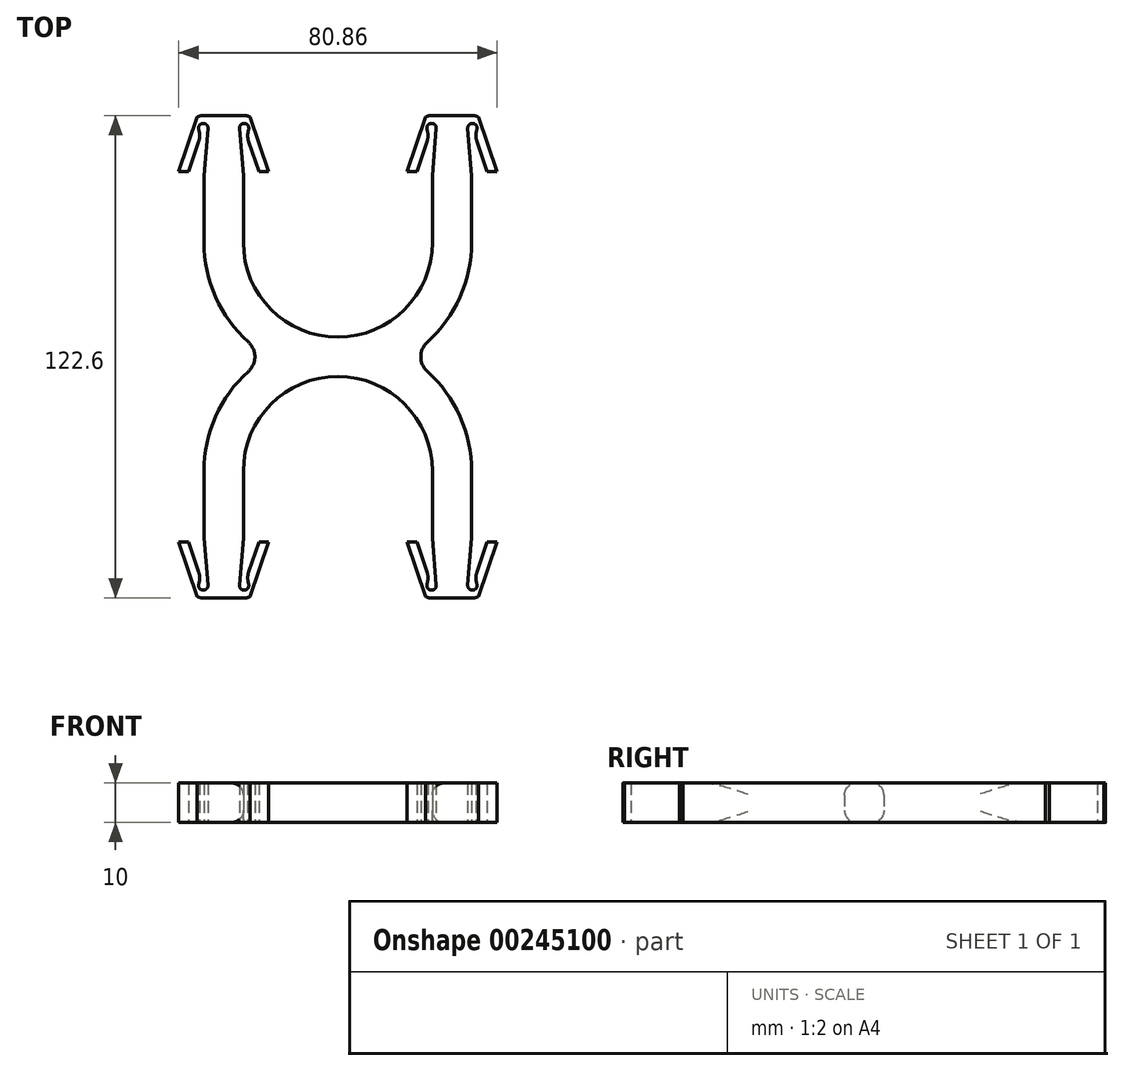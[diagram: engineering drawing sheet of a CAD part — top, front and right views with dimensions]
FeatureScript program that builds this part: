
annotation { "Feature Type Name" : "Feature", "Feature Type Description" : "" }
export const myFeature = defineFeature(function(context is Context, id is Id, definition is map)
    precondition{}
    {
        {
            var Q0;
            Q0=qCreatedBy(makeId("Top.planeOp"),FACE);
            var sketch = newSketch(context, id + "F0", { "sketchPlane" : qUnion([Q0])});
            skLineSegment(sketch, "E0", {"start": v(6.36, 8.63) * mm, "end": v(8.93, 1) * mm});
            skLineSegment(sketch, "E1", {"start": v(8.93, 1) * mm, "end": v(11.43, 1) * mm});
            skLineSegment(sketch, "E2", {"start": v(11.43, 1) * mm, "end": v(6.76, 14.9) * mm});
            skLineSegment(sketch, "E3", {"start": v(5.2, 15.3) * mm, "end": v(0, 15.3) * mm});
            skArc(sketch, "E4", {"start": v(6.34, 11.74) * mm, "mid": v(5.33, 13.3) * mm, "end": v(4, 12) * mm});
            skLineSegment(sketch, "E5", {"start": v(5, 0) * mm, "end": v(4, 12) * mm});
            skArc(sketch, "E6", {"start": v(5.2, 15.3) * mm, "mid": v(6, 15.2) * mm, "end": v(6.76, 14.9) * mm});
            skLineSegment(sketch, "E7.MirrorCS", {"start": v(-5.2, 15.3) * mm, "end": v(0, 15.3) * mm});
            skArc(sketch, "E8.MirrorCS", {"start": v(-5.2, 15.3) * mm, "mid": v(-6, 15.2) * mm, "end": v(-6.76, 14.9) * mm});
            skLineSegment(sketch, "E9.MirrorCS", {"start": v(-11.43, 1) * mm, "end": v(-6.76, 14.9) * mm});
            skLineSegment(sketch, "E10.MirrorCS", {"start": v(-8.93, 1) * mm, "end": v(-11.43, 1) * mm});
            skLineSegment(sketch, "E11.MirrorCS", {"start": v(-6.36, 8.63) * mm, "end": v(-8.93, 1) * mm});
            skArc(sketch, "E12.MirrorCS", {"start": v(-6.34, 11.74) * mm, "mid": v(-5.33, 13.3) * mm, "end": v(-4, 12) * mm});
            skLineSegment(sketch, "E13.MirrorCS", {"start": v(-5, 0) * mm, "end": v(-4, 12) * mm});
            skLineSegment(sketch, "E14", {"start": v(-5, 0) * mm, "end": v(-5, -17) * mm});
            skLineSegment(sketch, "E15.MirrorCS", {"start": v(5, 0) * mm, "end": v(5, -17) * mm});
            skArc(sketch, "E16", {"start": v(5, -17) * mm, "mid": v(29, -41) * mm, "end": v(53, -17) * mm});
            skArc(sketch, "E17", {"start": v(-5, -17) * mm, "mid": v(-2.06, -30.84) * mm, "end": v(6.27, -42.28) * mm});
            skLineSegment(sketch, "E18", {"start": v(29, -17) * mm, "end": v(29, -5.61) * mm, "construction": true});
            skLineSegment(sketch, "E19.MirrorCS", {"start": v(53, 0) * mm, "end": v(53, -17) * mm});
            skLineSegment(sketch, "E20.MirrorCS", {"start": v(63, 0) * mm, "end": v(63, -17) * mm});
            skLineSegment(sketch, "E21.MirrorCS", {"start": v(63, 0) * mm, "end": v(62, 12) * mm});
            skArc(sketch, "E22.MirrorCS", {"start": v(64.34, 11.74) * mm, "mid": v(63.33, 13.3) * mm, "end": v(62, 12) * mm});
            skLineSegment(sketch, "E23.MirrorCS", {"start": v(64.36, 8.63) * mm, "end": v(66.93, 1) * mm});
            skLineSegment(sketch, "E24.MirrorCS", {"start": v(66.93, 1) * mm, "end": v(69.43, 1) * mm});
            skLineSegment(sketch, "E25.MirrorCS", {"start": v(69.43, 1) * mm, "end": v(64.76, 14.9) * mm});
            skArc(sketch, "E26.MirrorCS", {"start": v(63.2, 15.3) * mm, "mid": v(64, 15.2) * mm, "end": v(64.76, 14.9) * mm});
            skLineSegment(sketch, "E27.MirrorCS", {"start": v(63.2, 15.3) * mm, "end": v(58, 15.3) * mm});
            skLineSegment(sketch, "E28.MirrorCS", {"start": v(52.8, 15.3) * mm, "end": v(58, 15.3) * mm});
            skArc(sketch, "E29.MirrorCS", {"start": v(52.8, 15.3) * mm, "mid": v(52, 15.2) * mm, "end": v(51.24, 14.9) * mm});
            skLineSegment(sketch, "E30.MirrorCS", {"start": v(46.57, 1) * mm, "end": v(51.24, 14.9) * mm});
            skLineSegment(sketch, "E31.MirrorCS", {"start": v(49.07, 1) * mm, "end": v(46.57, 1) * mm});
            skLineSegment(sketch, "E32.MirrorCS", {"start": v(51.64, 8.63) * mm, "end": v(49.07, 1) * mm});
            skArc(sketch, "E33.MirrorCS", {"start": v(51.66, 11.74) * mm, "mid": v(52.67, 13.3) * mm, "end": v(54, 12) * mm});
            skLineSegment(sketch, "E34.MirrorCS", {"start": v(53, 0) * mm, "end": v(54, 12) * mm});
            skPoint(sketch, "E35.visualSharp", {"position": v(5.58, 10.96) * mm});
            skArc(sketch, "E35.filletArc", {"start": v(6.34, 11.74) * mm, "mid": v(6.1, 10.18) * mm, "end": v(6.36, 8.63) * mm});
            skPoint(sketch, "E36.visualSharp", {"position": v(-5.58, 10.96) * mm});
            skArc(sketch, "E36.filletArc", {"start": v(-6.36, 8.63) * mm, "mid": v(-6.1, 10.18) * mm, "end": v(-6.34, 11.74) * mm});
            skPoint(sketch, "E37.visualSharp", {"position": v(52.42, 10.96) * mm});
            skArc(sketch, "E37.filletArc", {"start": v(51.64, 8.63) * mm, "mid": v(51.9, 10.18) * mm, "end": v(51.66, 11.74) * mm});
            skPoint(sketch, "E38.visualSharp", {"position": v(63.58, 10.96) * mm});
            skArc(sketch, "E38.filletArc", {"start": v(64.34, 11.74) * mm, "mid": v(64.1, 10.18) * mm, "end": v(64.36, 8.63) * mm});
            skLineSegment(sketch, "E39", {"start": v(29, -41) * mm, "end": v(29, -51) * mm, "construction": true});
            skLineSegment(sketch, "E40", {"start": v(29, -46) * mm, "end": v(34.41, -46) * mm, "construction": true});
            skArc(sketch, "E41.MirrorCS", {"start": v(-5, -75) * mm, "mid": v(-2.06, -61.16) * mm, "end": v(6.27, -49.72) * mm});
            skArc(sketch, "E42.MirrorCS", {"start": v(5, -75) * mm, "mid": v(29, -51) * mm, "end": v(53, -75) * mm});
            skLineSegment(sketch, "E43.MirrorCS", {"start": v(63, -92) * mm, "end": v(63, -75) * mm});
            skLineSegment(sketch, "E44.MirrorCS", {"start": v(63, -92) * mm, "end": v(62, -104) * mm});
            skArc(sketch, "E45.MirrorCS", {"start": v(64.34, -103.74) * mm, "mid": v(63.33, -105.3) * mm, "end": v(62, -104) * mm});
            skArc(sketch, "E46.MirrorCS", {"start": v(64.34, -103.74) * mm, "mid": v(64.1, -102.18) * mm, "end": v(64.36, -100.63) * mm});
            skLineSegment(sketch, "E47.MirrorCS", {"start": v(64.36, -100.63) * mm, "end": v(66.93, -93) * mm});
            skLineSegment(sketch, "E48.MirrorCS", {"start": v(66.93, -93) * mm, "end": v(69.43, -93) * mm});
            skLineSegment(sketch, "E49.MirrorCS", {"start": v(69.43, -93) * mm, "end": v(64.76, -106.9) * mm});
            skArc(sketch, "E50.MirrorCS", {"start": v(63.2, -107.3) * mm, "mid": v(64, -107.2) * mm, "end": v(64.76, -106.9) * mm});
            skLineSegment(sketch, "E51.MirrorCS", {"start": v(63.2, -107.3) * mm, "end": v(58, -107.3) * mm});
            skLineSegment(sketch, "E52.MirrorCS", {"start": v(52.8, -107.3) * mm, "end": v(58, -107.3) * mm});
            skArc(sketch, "E53.MirrorCS", {"start": v(52.8, -107.3) * mm, "mid": v(52, -107.2) * mm, "end": v(51.24, -106.9) * mm});
            skLineSegment(sketch, "E54.MirrorCS", {"start": v(46.57, -93) * mm, "end": v(51.24, -106.9) * mm});
            skLineSegment(sketch, "E55.MirrorCS", {"start": v(49.07, -93) * mm, "end": v(46.57, -93) * mm});
            skLineSegment(sketch, "E56.MirrorCS", {"start": v(51.64, -100.63) * mm, "end": v(49.07, -93) * mm});
            skArc(sketch, "E57.MirrorCS", {"start": v(51.64, -100.63) * mm, "mid": v(51.9, -102.18) * mm, "end": v(51.66, -103.74) * mm});
            skArc(sketch, "E58.MirrorCS", {"start": v(51.66, -103.74) * mm, "mid": v(52.67, -105.3) * mm, "end": v(54, -104) * mm});
            skLineSegment(sketch, "E59.MirrorCS", {"start": v(53, -92) * mm, "end": v(54, -104) * mm});
            skLineSegment(sketch, "E60.MirrorCS", {"start": v(53, -92) * mm, "end": v(53, -75) * mm});
            skLineSegment(sketch, "E61.MirrorCS", {"start": v(5, -92) * mm, "end": v(5, -75) * mm});
            skLineSegment(sketch, "E62.MirrorCS", {"start": v(5, -92) * mm, "end": v(4, -104) * mm});
            skArc(sketch, "E63.MirrorCS", {"start": v(6.34, -103.74) * mm, "mid": v(5.33, -105.3) * mm, "end": v(4, -104) * mm});
            skArc(sketch, "E64.MirrorCS", {"start": v(6.34, -103.74) * mm, "mid": v(6.1, -102.18) * mm, "end": v(6.36, -100.63) * mm});
            skLineSegment(sketch, "E65.MirrorCS", {"start": v(6.36, -100.63) * mm, "end": v(8.93, -93) * mm});
            skLineSegment(sketch, "E66.MirrorCS", {"start": v(8.93, -93) * mm, "end": v(11.43, -93) * mm});
            skArc(sketch, "E67.MirrorCS", {"start": v(5.2, -107.3) * mm, "mid": v(6, -107.2) * mm, "end": v(6.76, -106.9) * mm});
            skLineSegment(sketch, "E68.MirrorCS", {"start": v(5.2, -107.3) * mm, "end": v(0, -107.3) * mm});
            skLineSegment(sketch, "E69.MirrorCS", {"start": v(-5.2, -107.3) * mm, "end": v(0, -107.3) * mm});
            skArc(sketch, "E70.MirrorCS", {"start": v(-5.2, -107.3) * mm, "mid": v(-6, -107.2) * mm, "end": v(-6.76, -106.9) * mm});
            skLineSegment(sketch, "E71.MirrorCS", {"start": v(-11.43, -93) * mm, "end": v(-6.76, -106.9) * mm});
            skLineSegment(sketch, "E72.MirrorCS", {"start": v(-8.93, -93) * mm, "end": v(-11.43, -93) * mm});
            skLineSegment(sketch, "E73.MirrorCS", {"start": v(-6.36, -100.63) * mm, "end": v(-8.93, -93) * mm});
            skArc(sketch, "E74.MirrorCS", {"start": v(-6.36, -100.63) * mm, "mid": v(-6.1, -102.18) * mm, "end": v(-6.34, -103.74) * mm});
            skArc(sketch, "E75.MirrorCS", {"start": v(-6.34, -103.74) * mm, "mid": v(-5.33, -105.3) * mm, "end": v(-4, -104) * mm});
            skLineSegment(sketch, "E76.MirrorCS", {"start": v(-5, -92) * mm, "end": v(-4, -104) * mm});
            skLineSegment(sketch, "E77.MirrorCS", {"start": v(-5, -92) * mm, "end": v(-5, -75) * mm});
            skLineSegment(sketch, "E78.MirrorCS", {"start": v(11.43, -93) * mm, "end": v(6.76, -106.9) * mm});
            skArc(sketch, "E79.trimOffspring", {"start": v(51.73, -49.72) * mm, "mid": v(60.06, -61.16) * mm, "end": v(63, -75) * mm});
            skArc(sketch, "E80.trimOffspring", {"start": v(51.73, -42.28) * mm, "mid": v(60.06, -30.84) * mm, "end": v(63, -17) * mm});
            skPoint(sketch, "E81.visualSharp", {"position": v(11.25, -46) * mm});
            skArc(sketch, "E81.filletArc", {"start": v(6.27, -49.72) * mm, "mid": v(7.92, -46) * mm, "end": v(6.27, -42.28) * mm});
            skPoint(sketch, "E82.visualSharp", {"position": v(46.75, -46) * mm});
            skArc(sketch, "E82.filletArc", {"start": v(51.73, -42.28) * mm, "mid": v(50.08, -46) * mm, "end": v(51.73, -49.72) * mm});
            skSolve(sketch);
        }
        {
            var Q0;
            Q0 = qSketchRegion(id + "F0", true);
            extrude(context, id + "F1", {"entities" : qUnion([Q0]), "depth" : 10 * mm});
        }
        {
            var Q0;
            Q0=makeQuery(id+"F1.opExtrude","CAP_EDGE",EDGE,{"disambiguationData":[OSD([sQuery(id+"F0.wireOp",EDGE,"E16")])],"isStart":false});
            var Q1;
            Q1=makeQuery(id+"F1.opExtrude","CAP_EDGE",EDGE,{"disambiguationData":[OSD([sQuery(id+"F0.wireOp",EDGE,"E16")])],"isStart":true});
            var Q2;
            Q2=makeQuery(id+"F1.opExtrude","CAP_EDGE",EDGE,{"disambiguationData":[OSD([sQuery(id+"F0.wireOp",EDGE,"E42.MirrorCS")])],"isStart":false});
            var Q3;
            Q3=makeQuery(id+"F1.opExtrude","CAP_EDGE",EDGE,{"disambiguationData":[OSD([sQuery(id+"F0.wireOp",EDGE,"E42.MirrorCS")])],"isStart":true});
            fillet(context, id + "F2", {"entities" : qUnion([Q0, Q1, Q2, Q3]), "radius" : 3 * mm, "allowEdgeOverflow" : false});
        }
    });
